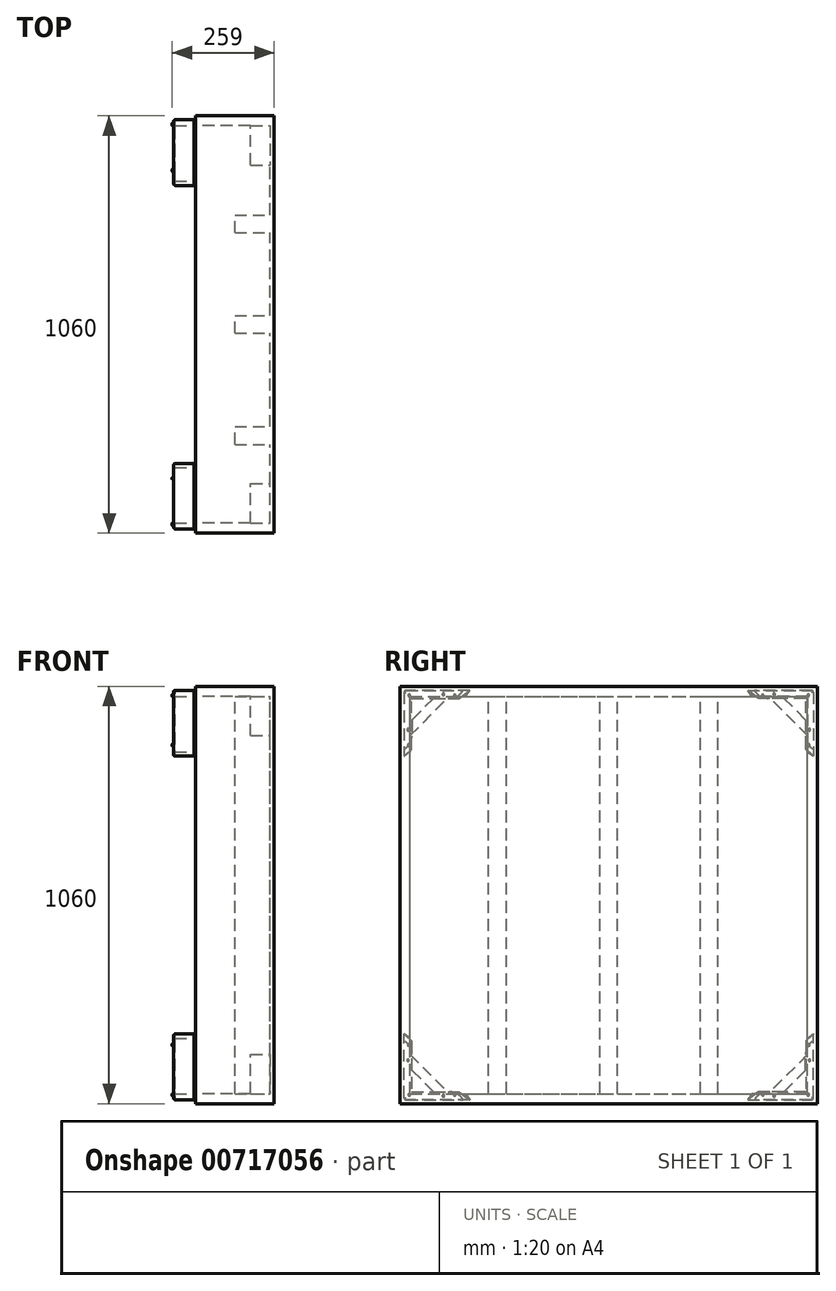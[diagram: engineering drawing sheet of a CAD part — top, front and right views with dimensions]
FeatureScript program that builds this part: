
annotation { "Feature Type Name" : "Feature", "Feature Type Description" : "" }
export const myFeature = defineFeature(function(context is Context, id is Id, definition is map)
    precondition{}
    {
        {
            var Q0;
            Q0=qCreatedBy(makeId("Right.planeOp"),FACE);
            var sketch = newSketch(context, id + "F0", { "sketchPlane" : qUnion([Q0])});
            skLineSegment(sketch, "E0.bottom", {"start": v(530, -530) * mm, "end": v(-530, -530) * mm});
            skLineSegment(sketch, "E0.top", {"start": v(530, 530) * mm, "end": v(-530, 530) * mm});
            skLineSegment(sketch, "E0.left", {"start": v(530, -530) * mm, "end": v(530, 530) * mm});
            skLineSegment(sketch, "E0.right", {"start": v(-530, -530) * mm, "end": v(-530, 530) * mm});
            skPoint(sketch, "E0.middle", {"position": v(0, 0) * mm});
            skSolve(sketch);
        }
        {
            var Q0;
            Q0 = qSketchRegion(id + "F0", true);
            extrude(context, id + "F1", {"entities" : qUnion([Q0]), "depth" : 200 * mm, "offsetDistance" : 25 * mm});
        }
        {
            var Q0;
            Q0=makeQuery(id+"F1.opExtrude","CAP_FACE",FACE,{"disambiguationData":[OSD([sQuery(id+"F0.wireOp",EDGE,"E0.bottom"),sQuery(id+"F0.wireOp",EDGE,"E0.top"),sQuery(id+"F0.wireOp",EDGE,"E0.left"),sQuery(id+"F0.wireOp",EDGE,"E0.right")])],"isStart":true});
            var sketch = newSketch(context, id + "F2", { "sketchPlane" : qUnion([Q0])});
            skLineSegment(sketch, "E1.bottom", {"start": v(505, -505) * mm, "end": v(-505, -505) * mm});
            skLineSegment(sketch, "E1.top", {"start": v(505, 505) * mm, "end": v(-505, 505) * mm});
            skLineSegment(sketch, "E1.left", {"start": v(505, -505) * mm, "end": v(505, 505) * mm});
            skLineSegment(sketch, "E1.right", {"start": v(-505, -505) * mm, "end": v(-505, 505) * mm});
            skPoint(sketch, "E1.middle", {"position": v(0, 0) * mm});
            skSolve(sketch);
        }
        {
            var Q0;
            Q0 = qSketchRegion(id + "F2", true);
            extrude(context, id + "F3", {"entities" : qUnion([Q0]), "operationType" : NewBodyOperationType.REMOVE, "oppositeDirection" : true, "depth" : 190 * mm, "offsetDistance" : 25 * mm});
        }
        {
            var Q0;
            Q0=makeQuery(id+"F3.boolean.opBoolean","COPY",FACE,{"derivedFrom":makeQuery(id+"F3.opExtrude","CAP_FACE",FACE,{"disambiguationData":[OSD([sQuery(id+"F2.wireOp",EDGE,"E1.bottom"),sQuery(id+"F2.wireOp",EDGE,"E1.top"),sQuery(id+"F2.wireOp",EDGE,"E1.left"),sQuery(id+"F2.wireOp",EDGE,"E1.right")])],"isStart":false})});
            var sketch = newSketch(context, id + "F4", { "sketchPlane" : qUnion([Q0])});
            skLineSegment(sketch, "E2", {"start": v(0, 505) * mm, "end": v(0, -505) * mm, "construction": true});
            skLineSegment(sketch, "E3", {"start": v(-505, 0) * mm, "end": v(505, 0) * mm, "construction": true});
            skLineSegment(sketch, "E4", {"start": v(-505, 405) * mm, "end": v(-405, 505) * mm});
            skLineSegment(sketch, "E5", {"start": v(-405, 505) * mm, "end": v(-505, 505) * mm});
            skLineSegment(sketch, "E6", {"start": v(-505, 505) * mm, "end": v(-505, 405) * mm});
            skLineSegment(sketch, "E7.MirrorCS", {"start": v(505, 405) * mm, "end": v(405, 505) * mm});
            skLineSegment(sketch, "E8.MirrorCS", {"start": v(405, 505) * mm, "end": v(505, 505) * mm});
            skLineSegment(sketch, "E9.MirrorCS", {"start": v(505, 505) * mm, "end": v(505, 405) * mm});
            skLineSegment(sketch, "E10.MirrorCS", {"start": v(-505, -405) * mm, "end": v(-405, -505) * mm});
            skLineSegment(sketch, "E11.MirrorCS", {"start": v(-405, -505) * mm, "end": v(-505, -505) * mm});
            skLineSegment(sketch, "E12.MirrorCS", {"start": v(-505, -505) * mm, "end": v(-505, -405) * mm});
            skLineSegment(sketch, "E13.MirrorCS", {"start": v(505, -405) * mm, "end": v(405, -505) * mm});
            skLineSegment(sketch, "E14.MirrorCS", {"start": v(405, -505) * mm, "end": v(505, -505) * mm});
            skLineSegment(sketch, "E15.MirrorCS", {"start": v(505, -505) * mm, "end": v(505, -405) * mm});
            skSolve(sketch);
        }
        {
            var Q0;
            Q0 = qSketchRegion(id + "F4", true);
            extrude(context, id + "F5", {"entities" : qUnion([Q0]), "operationType" : NewBodyOperationType.ADD, "depth" : 50 * mm, "offsetDistance" : 25 * mm});
        }
        {
            var Q0;
            Q0=makeQuery(id+"F5.boolean.opBoolean","MERGE",FACE,{"derivedFrom":[makeQuery(id+"F1.opExtrude","CAP_FACE",FACE,{"disambiguationData":[OSD([sQuery(id+"F0.wireOp",EDGE,"E0.bottom"),sQuery(id+"F0.wireOp",EDGE,"E0.top"),sQuery(id+"F0.wireOp",EDGE,"E0.left"),sQuery(id+"F0.wireOp",EDGE,"E0.right")])],"isStart":true}),makeQuery(id+"F5.opExtrude","CAP_FACE",FACE,{"disambiguationData":[OSD([sQuery(id+"F4.wireOp",EDGE,"E4"),sQuery(id+"F4.wireOp",EDGE,"E5"),sQuery(id+"F4.wireOp",EDGE,"E6")])],"isStart":false}),makeQuery(id+"F5.opExtrude","CAP_FACE",FACE,{"disambiguationData":[OSD([sQuery(id+"F4.wireOp",EDGE,"E7.MirrorCS"),sQuery(id+"F4.wireOp",EDGE,"E8.MirrorCS"),sQuery(id+"F4.wireOp",EDGE,"E9.MirrorCS")])],"isStart":false}),makeQuery(id+"F5.opExtrude","CAP_FACE",FACE,{"disambiguationData":[OSD([sQuery(id+"F4.wireOp",EDGE,"E10.MirrorCS"),sQuery(id+"F4.wireOp",EDGE,"E11.MirrorCS"),sQuery(id+"F4.wireOp",EDGE,"E12.MirrorCS")])],"isStart":false}),makeQuery(id+"F5.opExtrude","CAP_FACE",FACE,{"disambiguationData":[OSD([sQuery(id+"F4.wireOp",EDGE,"E13.MirrorCS"),sQuery(id+"F4.wireOp",EDGE,"E14.MirrorCS"),sQuery(id+"F4.wireOp",EDGE,"E15.MirrorCS")])],"isStart":false})]});
            var sketch = newSketch(context, id + "F6", { "sketchPlane" : qUnion([Q0])});
            skLineSegment(sketch, "E16", {"start": v(-520, 520) * mm, "end": v(-370, 520) * mm});
            skLineSegment(sketch, "E17", {"start": v(-520, 520) * mm, "end": v(-520, 370) * mm});
            skLineSegment(sketch, "E18", {"start": v(-500, 445) * mm, "end": v(-500, 404.8) * mm});
            skLineSegment(sketch, "E19", {"start": v(-520, 370) * mm, "end": v(-517.3, 371.86) * mm});
            skPoint(sketch, "E20.visualSharp", {"position": v(-500, 383.78) * mm});
            skArc(sketch, "E20.filletArc", {"start": v(-517.3, 371.86) * mm, "mid": v(-504.59, 386.2) * mm, "end": v(-500, 404.8) * mm});
            skLineSegment(sketch, "E21", {"start": v(-520, 520) * mm, "end": v(-344.75, 344.75) * mm, "construction": true});
            skLineSegment(sketch, "E22.MirrorCS", {"start": v(-445, 500) * mm, "end": v(-404.8, 500) * mm});
            skArc(sketch, "E23.MirrorCS", {"start": v(-371.86, 517.3) * mm, "mid": v(-386.2, 504.59) * mm, "end": v(-404.8, 500) * mm});
            skLineSegment(sketch, "E24", {"start": v(-371.86, 517.3) * mm, "end": v(-370, 520) * mm});
            skLineSegment(sketch, "E25", {"start": v(-445, 500) * mm, "end": v(-500, 445) * mm});
            skLineSegment(sketch, "E26", {"start": v(0, 530) * mm, "end": v(0, -530) * mm, "construction": true});
            skLineSegment(sketch, "E27", {"start": v(530, 0) * mm, "end": v(-530, 0) * mm, "construction": true});
            skSolve(sketch);
        }
        {
            var Q0;
            Q0 = qSketchRegion(id + "F6", true);
            extrude(context, id + "F7", {"entities" : qUnion([Q0]), "operationType" : NewBodyOperationType.ADD, "depth" : 3 * mm, "offsetDistance" : 25 * mm});
        }
        {
            var Q0;
            Q0=makeQuery(id+"F7.opExtrude","CAP_FACE",FACE,{"disambiguationData":[OSD([sQuery(id+"F6.wireOp",EDGE,"E16"),sQuery(id+"F6.wireOp",EDGE,"E17"),sQuery(id+"F6.wireOp",EDGE,"E18"),sQuery(id+"F6.wireOp",EDGE,"E19"),sQuery(id+"F6.wireOp",EDGE,"E20.filletArc"),sQuery(id+"F6.wireOp",EDGE,"E22.MirrorCS"),sQuery(id+"F6.wireOp",EDGE,"E23.MirrorCS"),sQuery(id+"F6.wireOp",EDGE,"E24"),sQuery(id+"F6.wireOp",EDGE,"E25")])],"isStart":false});
            var sketch = newSketch(context, id + "F8", { "sketchPlane" : qUnion([Q0])});
            skCircle(sketch, "E28", {"center": v(-510, 420) * mm, "radius": 2.75 * mm});
            skCircle(sketch, "E29", {"center": v(-420, 510) * mm, "radius": 3.18 * mm});
            skCircle(sketch, "E30.MirrorC", {"center": v(510, 420) * mm, "radius": 2.75 * mm});
            skCircle(sketch, "E31.MirrorC", {"center": v(420, 510) * mm, "radius": 3.18 * mm});
            skSolve(sketch);
        }
        {
            var Q0;
            Q0=makeQuery(id+"F8.imprint","IMPRINT",FACE,{"disambiguationData":[TD([[makeQuery(id+"F8.imprint","IMPRINT",EDGE,{"derivedFrom":sQuery(id+"F8.wireOp",EDGE,"E28")}),1.0]])]});
            var Q1;
            Q1=makeQuery(id+"F8.imprint","IMPRINT",FACE,{"disambiguationData":[TD([[makeQuery(id+"F8.imprint","IMPRINT",EDGE,{"derivedFrom":sQuery(id+"F8.wireOp",EDGE,"E29")}),1.0]])]});
            extrude(context, id + "F9", {"entities" : qUnion([Q0, Q1]), "operationType" : NewBodyOperationType.REMOVE, "oppositeDirection" : true, "depth" : 25 * mm, "offsetDistance" : 25 * mm});
        }
        {
            var Q0;
            Q0=makeQuery(id+"F7.opExtrude","CAP_FACE",FACE,{"disambiguationData":[OSD([sQuery(id+"F6.wireOp",EDGE,"E16"),sQuery(id+"F6.wireOp",EDGE,"E17"),sQuery(id+"F6.wireOp",EDGE,"E18"),sQuery(id+"F6.wireOp",EDGE,"E19"),sQuery(id+"F6.wireOp",EDGE,"E20.filletArc"),sQuery(id+"F6.wireOp",EDGE,"E22.MirrorCS"),sQuery(id+"F6.wireOp",EDGE,"E23.MirrorCS"),sQuery(id+"F6.wireOp",EDGE,"E24"),sQuery(id+"F6.wireOp",EDGE,"E25")])],"isStart":false});
            var sketch = newSketch(context, id + "F10", { "sketchPlane" : qUnion([Q0])});
            skLineSegment(sketch, "E32", {"start": v(0, 0) * mm, "end": v(0, 553) * mm});
            skLineSegment(sketch, "E33", {"start": v(0, 553) * mm, "end": v(0, -610.23) * mm, "construction": true});
            skLineSegment(sketch, "E34", {"start": v(0, 0) * mm, "end": v(-602.07, 0) * mm});
            skLineSegment(sketch, "E35", {"start": v(-602.07, 0) * mm, "end": v(591.35, 0) * mm, "construction": true});
            skSolve(sketch);
        }
        {
            var Q0;
            Q0=makeQuery(id+"F10.imprint","IMPRINT",FACE,{"disambiguationData":[TD([[makeQuery(id+"F10.imprint","IMPRINT",EDGE,{"derivedFrom":makeQuery(id+"F7.opExtrude","CAP_EDGE",EDGE,{"disambiguationData":[OSD([sQuery(id+"F6.wireOp",EDGE,"E16")])],"isStart":false})}),-1.0]])]});
            var sketch = newSketch(context, id + "F11", { "sketchPlane" : qUnion([Q0])});
            skLineSegment(sketch, "E36", {"start": v(-504.96, 505.02) * mm, "end": v(-363.52, 505.02) * mm});
            skLineSegment(sketch, "E37", {"start": v(-363.52, 505.02) * mm, "end": v(-353.08, 520.03) * mm});
            skLineSegment(sketch, "E38", {"start": v(-353.08, 520.03) * mm, "end": v(-519.88, 520.11) * mm});
            skLineSegment(sketch, "E39", {"start": v(-519.88, 520.11) * mm, "end": v(-519.97, 352.84) * mm});
            skLineSegment(sketch, "E40", {"start": v(-504.96, 505.02) * mm, "end": v(-505.04, 363.57) * mm});
            skLineSegment(sketch, "E41", {"start": v(-505.04, 363.57) * mm, "end": v(-519.97, 352.84) * mm});
            skSolve(sketch);
        }
        {
            var Q0;
            Q0 = qSketchRegion(id + "F11", true);
            extrude(context, id + "F12", {"entities" : qUnion([Q0]), "operationType" : NewBodyOperationType.ADD, "depth" : 50 * mm, "offsetDistance" : 25 * mm});
        }
        {
            var Q0;
            Q0=makeQuery(id+"F12.opExtrude","CAP_FACE",FACE,{"disambiguationData":[OSD([sQuery(id+"F11.wireOp",EDGE,"E36"),sQuery(id+"F11.wireOp",EDGE,"E37"),sQuery(id+"F11.wireOp",EDGE,"E38"),sQuery(id+"F11.wireOp",EDGE,"E39"),sQuery(id+"F11.wireOp",EDGE,"E40"),sQuery(id+"F11.wireOp",EDGE,"E41")])],"isStart":false});
            var sketch = newSketch(context, id + "F13", { "sketchPlane" : qUnion([Q0])});
            skLineSegment(sketch, "E42", {"start": v(-519.97, 352.84) * mm, "end": v(-500.96, 370.22) * mm});
            skLineSegment(sketch, "E43", {"start": v(-500.96, 370.22) * mm, "end": v(-500.96, 500.08) * mm});
            skLineSegment(sketch, "E44", {"start": v(-500.96, 500.08) * mm, "end": v(-380.13, 500.08) * mm});
            skLineSegment(sketch, "E45", {"start": v(-380.13, 500.08) * mm, "end": v(-353.08, 520.03) * mm});
            skLineSegment(sketch, "E46", {"start": v(-353.08, 520.03) * mm, "end": v(-519.88, 520.11) * mm});
            skLineSegment(sketch, "E47", {"start": v(-519.88, 520.11) * mm, "end": v(-519.97, 352.84) * mm});
            skSolve(sketch);
        }
        {
            var Q0;
            Q0 = qSketchRegion(id + "F13", true);
            extrude(context, id + "F14", {"entities" : qUnion([Q0]), "operationType" : NewBodyOperationType.ADD, "depth" : 3 * mm, "offsetDistance" : 25 * mm});
        }
        {
            var Q0;
            Q0=makeQuery(id+"F14.opExtrude","CAP_EDGE",EDGE,{"disambiguationData":[OSD([sQuery(id+"F13.wireOp",EDGE,"E46")])],"isStart":false});
            var Q1;
            Q1=makeQuery(id+"F14.opExtrude","CAP_EDGE",EDGE,{"disambiguationData":[OSD([sQuery(id+"F13.wireOp",EDGE,"E47")])],"isStart":false});
            var Q2;
            Q2=makeQuery(id+"F14.boolean.opBoolean","MERGE",EDGE,{"derivedFrom":[makeQuery(id+"F12.opExtrude","SWEPT_EDGE",EDGE,{"disambiguationData":[OSD([sQuery(id+"F11.wireOp",EDGE,"E38"),sQuery(id+"F11.wireOp",EDGE,"E39")])]}),makeQuery(id+"F14.opExtrude","SWEPT_EDGE",EDGE,{"disambiguationData":[OSD([sQuery(id+"F13.wireOp",EDGE,"E46"),sQuery(id+"F13.wireOp",EDGE,"E47")])]})]});
            fillet(context, id + "F15", {"entities" : qUnion([Q0, Q1, Q2]), "radius" : 5 * mm, "tangentPropagation" : true, "allowEdgeOverflow" : false});
        }
        {
            var Q0;
            Q0=makeQuery(id+"F10.imprint","IMPRINT",FACE,{"disambiguationData":[TD([[makeQuery(id+"F10.imprint","IMPRINT",EDGE,{"derivedFrom":makeQuery(id+"F7.opExtrude","CAP_EDGE",EDGE,{"disambiguationData":[OSD([sQuery(id+"F6.wireOp",EDGE,"E16")])],"isStart":false})}),-1.0]])]});
            var sketch = newSketch(context, id + "F16", { "sketchPlane" : qUnion([Q0])});
            skCircle(sketch, "E48", {"center": v(-468.4, 468.74) * mm, "radius": 2.77 * mm});
            skSolve(sketch);
        }
        {
            var Q0;
            Q0 = qSketchRegion(id + "F16", true);
            extrude(context, id + "F17", {"entities" : qUnion([Q0]), "operationType" : NewBodyOperationType.REMOVE, "oppositeDirection" : true, "depth" : 25 * mm, "offsetDistance" : 25 * mm});
        }
        {
            var Q0;
            Q0=makeQuery(id+"F1.opExtrude","SWEPT_BODY",BODY,{"disambiguationData":[OSD([sQuery(id+"F0.wireOp",EDGE,"E0.bottom"),sQuery(id+"F0.wireOp",EDGE,"E0.top"),sQuery(id+"F0.wireOp",EDGE,"E0.left"),sQuery(id+"F0.wireOp",EDGE,"E0.right")])]});
            var Q1;
            Q1=qCreatedBy(makeId("Front.planeOp"),FACE);
            mirror(context, id + "F18", {"operationType" : NewBodyOperationType.ADD, "entities" : qUnion([Q0]), "mirrorPlane" : qUnion([Q1])});
        }
        {
            var Q0;
            Q0=makeQuery(id+"F1.opExtrude","SWEPT_BODY",BODY,{"disambiguationData":[OSD([sQuery(id+"F0.wireOp",EDGE,"E0.bottom"),sQuery(id+"F0.wireOp",EDGE,"E0.top"),sQuery(id+"F0.wireOp",EDGE,"E0.left"),sQuery(id+"F0.wireOp",EDGE,"E0.right")])]});
            var Q1;
            Q1=qCreatedBy(makeId("Top.planeOp"),FACE);
            mirror(context, id + "F19", {"operationType" : NewBodyOperationType.ADD, "entities" : qUnion([Q0]), "mirrorPlane" : qUnion([Q1])});
        }
        {
            var Q0;
            Q0=makeQuery(id+"F3.boolean.opBoolean","COPY",FACE,{"derivedFrom":makeQuery(id+"F3.opExtrude","CAP_FACE",FACE,{"disambiguationData":[OSD([sQuery(id+"F2.wireOp",EDGE,"E1.bottom"),sQuery(id+"F2.wireOp",EDGE,"E1.top"),sQuery(id+"F2.wireOp",EDGE,"E1.left"),sQuery(id+"F2.wireOp",EDGE,"E1.right")])],"isStart":false})});
            var sketch = newSketch(context, id + "F20", { "sketchPlane" : qUnion([Q0])});
            skLineSegment(sketch, "E49.bottom", {"start": v(22.5, -505) * mm, "end": v(-22.5, -505) * mm});
            skLineSegment(sketch, "E49.top", {"start": v(22.5, 505) * mm, "end": v(-22.5, 505) * mm});
            skLineSegment(sketch, "E49.left", {"start": v(22.5, -505) * mm, "end": v(22.5, 505) * mm});
            skLineSegment(sketch, "E49.right", {"start": v(-22.5, -505) * mm, "end": v(-22.5, 505) * mm});
            skPoint(sketch, "E49.middle", {"position": v(0, 0) * mm});
            skLineSegment(sketch, "E50.bottom", {"start": v(305, -505) * mm, "end": v(260, -505) * mm});
            skLineSegment(sketch, "E50.top", {"start": v(305, 505) * mm, "end": v(260, 505) * mm});
            skLineSegment(sketch, "E50.left", {"start": v(305, -505) * mm, "end": v(305, 505) * mm});
            skLineSegment(sketch, "E50.right", {"start": v(260, -505) * mm, "end": v(260, 505) * mm});
            skPoint(sketch, "E50.middle", {"position": v(282.5, 0) * mm});
            skLineSegment(sketch, "E51.bottom", {"start": v(-232.5, -505) * mm, "end": v(-277.5, -505) * mm});
            skLineSegment(sketch, "E51.top", {"start": v(-232.5, 505) * mm, "end": v(-277.5, 505) * mm});
            skLineSegment(sketch, "E51.left", {"start": v(-232.5, -505) * mm, "end": v(-232.5, 505) * mm});
            skLineSegment(sketch, "E51.right", {"start": v(-277.5, -505) * mm, "end": v(-277.5, 505) * mm});
            skPoint(sketch, "E51.middle", {"position": v(-255, 0) * mm});
            skSolve(sketch);
        }
        {
            var Q0;
            Q0 = qSketchRegion(id + "F20", true);
            extrude(context, id + "F21", {"entities" : qUnion([Q0]), "operationType" : NewBodyOperationType.ADD, "depth" : 90 * mm, "offsetDistance" : 25 * mm});
        }
        {
            var Q0;
            Q0=makeQuery(id+"F18.opPattern","COPY",FACE,{"derivedFrom":makeQuery(id+"F14.opExtrude","CAP_FACE",FACE,{"disambiguationData":[OSD([sQuery(id+"F13.wireOp",EDGE,"E42"),sQuery(id+"F13.wireOp",EDGE,"E43"),sQuery(id+"F13.wireOp",EDGE,"E44"),sQuery(id+"F13.wireOp",EDGE,"E45"),sQuery(id+"F13.wireOp",EDGE,"E46"),sQuery(id+"F13.wireOp",EDGE,"E47")])],"isStart":false}),"instanceName":"1"});
            var sketch = newSketch(context, id + "F22", { "sketchPlane" : qUnion([Q0])});
            skCircle(sketch, "E52", {"center": v(391.23, 507.06) * mm, "radius": 3 * mm});
            skCircle(sketch, "E53", {"center": v(506.83, 507.3) * mm, "radius": 3 * mm});
            skCircle(sketch, "E54", {"center": v(508.54, 380.79) * mm, "radius": 3 * mm});
            skCircle(sketch, "E55.MirrorC", {"center": v(-391.23, 507.06) * mm, "radius": 3 * mm});
            skCircle(sketch, "E56.MirrorC", {"center": v(-506.83, 507.3) * mm, "radius": 3 * mm});
            skCircle(sketch, "E57.MirrorC", {"center": v(-508.54, 380.79) * mm, "radius": 3 * mm});
            skCircle(sketch, "E58.MirrorC", {"center": v(-508.54, -380.79) * mm, "radius": 3 * mm});
            skCircle(sketch, "E59.MirrorC", {"center": v(-506.83, -507.3) * mm, "radius": 3 * mm});
            skCircle(sketch, "E60.MirrorC", {"center": v(-391.23, -507.06) * mm, "radius": 3 * mm});
            skCircle(sketch, "E61.MirrorC", {"center": v(508.54, -380.79) * mm, "radius": 3 * mm});
            skCircle(sketch, "E62.MirrorC", {"center": v(506.83, -507.3) * mm, "radius": 3 * mm});
            skCircle(sketch, "E63.MirrorC", {"center": v(391.23, -507.06) * mm, "radius": 3 * mm});
            skSolve(sketch);
        }
        {
            var Q0;
            Q0 = qSketchRegion(id + "F22", true);
            extrude(context, id + "F23", {"entities" : qUnion([Q0]), "operationType" : NewBodyOperationType.ADD, "depth" : 3 * mm, "offsetDistance" : 25 * mm, "hasDraft" : true, "draftAngle" : 3 * degree, "draftPullDirection" : true});
        }
        {
            var Q0;
            Q0=makeQuery(id+"F23.opExtrude","CAP_EDGE",EDGE,{"disambiguationData":[OSD([sQuery(id+"F22.wireOp",EDGE,"E63.MirrorC")])],"isStart":false});
            var Q1;
            Q1=makeQuery(id+"F23.opExtrude","CAP_EDGE",EDGE,{"disambiguationData":[OSD([sQuery(id+"F22.wireOp",EDGE,"E62.MirrorC")])],"isStart":false});
            var Q2;
            Q2=makeQuery(id+"F23.opExtrude","CAP_EDGE",EDGE,{"disambiguationData":[OSD([sQuery(id+"F22.wireOp",EDGE,"E61.MirrorC")])],"isStart":false});
            var Q3;
            Q3=makeQuery(id+"F23.opExtrude","CAP_EDGE",EDGE,{"disambiguationData":[OSD([sQuery(id+"F22.wireOp",EDGE,"E54")])],"isStart":false});
            var Q4;
            Q4=makeQuery(id+"F23.opExtrude","CAP_EDGE",EDGE,{"disambiguationData":[OSD([sQuery(id+"F22.wireOp",EDGE,"E53")])],"isStart":false});
            var Q5;
            Q5=makeQuery(id+"F23.opExtrude","CAP_EDGE",EDGE,{"disambiguationData":[OSD([sQuery(id+"F22.wireOp",EDGE,"E52")])],"isStart":false});
            var Q6;
            Q6=makeQuery(id+"F23.opExtrude","CAP_EDGE",EDGE,{"disambiguationData":[OSD([sQuery(id+"F22.wireOp",EDGE,"E55.MirrorC")])],"isStart":false});
            var Q7;
            Q7=makeQuery(id+"F23.opExtrude","CAP_EDGE",EDGE,{"disambiguationData":[OSD([sQuery(id+"F22.wireOp",EDGE,"E56.MirrorC")])],"isStart":false});
            var Q8;
            Q8=makeQuery(id+"F23.opExtrude","CAP_EDGE",EDGE,{"disambiguationData":[OSD([sQuery(id+"F22.wireOp",EDGE,"E57.MirrorC")])],"isStart":false});
            var Q9;
            Q9=makeQuery(id+"F23.opExtrude","CAP_EDGE",EDGE,{"disambiguationData":[OSD([sQuery(id+"F22.wireOp",EDGE,"E60.MirrorC")])],"isStart":false});
            var Q10;
            Q10=makeQuery(id+"F23.opExtrude","CAP_EDGE",EDGE,{"disambiguationData":[OSD([sQuery(id+"F22.wireOp",EDGE,"E59.MirrorC")])],"isStart":false});
            var Q11;
            Q11=makeQuery(id+"F23.opExtrude","CAP_EDGE",EDGE,{"disambiguationData":[OSD([sQuery(id+"F22.wireOp",EDGE,"E58.MirrorC")])],"isStart":false});
            fillet(context, id + "F24", {"entities" : qUnion([Q0, Q1, Q2, Q3, Q4, Q5, Q6, Q7, Q8, Q9, Q10, Q11]), "radius" : 1 * mm, "tangentPropagation" : true, "allowEdgeOverflow" : false});
        }
        {
            var Q0;
            Q0=makeQuery(id+"F7.opExtrude","SWEPT_EDGE",EDGE,{"disambiguationData":[OSD([sQuery(id+"F6.wireOp",EDGE,"E16"),sQuery(id+"F6.wireOp",EDGE,"E17")])]});
            var Q1;
            Q1=makeQuery(id+"F18.opPattern","COPY",EDGE,{"derivedFrom":makeQuery(id+"F7.opExtrude","SWEPT_EDGE",EDGE,{"disambiguationData":[OSD([sQuery(id+"F6.wireOp",EDGE,"E16"),sQuery(id+"F6.wireOp",EDGE,"E17")])]}),"instanceName":"1"});
            var Q2;
            {var subQ0=sQuery(id+"F13.wireOp",EDGE,"E47");Q2=makeQuery(id+"F18.opPattern","COPY",EDGE,{"derivedFrom":makeQuery(id+"F15.opFillet","BLEND_EDGE",EDGE,{"blendedFrom":[makeQuery(id+"F14.opExtrude","CAP_EDGE",EDGE,{"disambiguationData":[OSD([subQ0])],"isStart":false}),makeQuery(id+"F14.opExtrude","CAP_FACE",FACE,{"disambiguationData":[OSD([sQuery(id+"F13.wireOp",EDGE,"E42"),sQuery(id+"F13.wireOp",EDGE,"E43"),sQuery(id+"F13.wireOp",EDGE,"E44"),sQuery(id+"F13.wireOp",EDGE,"E45"),sQuery(id+"F13.wireOp",EDGE,"E46"),subQ0])],"isStart":false})],"blendedInto":[makeQuery(id+"F14.opExtrude","CAP_FACE",FACE,{"disambiguationData":[OSD([sQuery(id+"F13.wireOp",EDGE,"E42"),sQuery(id+"F13.wireOp",EDGE,"E43"),sQuery(id+"F13.wireOp",EDGE,"E44"),sQuery(id+"F13.wireOp",EDGE,"E45"),sQuery(id+"F13.wireOp",EDGE,"E46"),subQ0])],"isStart":false})]}),"instanceName":"1"});}
            var Q3;
            Q3=makeQuery(id+"F23.opExtrude","CAP_EDGE",EDGE,{"disambiguationData":[OSD([sQuery(id+"F22.wireOp",EDGE,"E54")])],"isStart":true});
            var Q4;
            {var subQ0=sQuery(id+"F22.wireOp",EDGE,"E54");Q4=makeQuery(id+"F24.opFillet","BLEND_EDGE",EDGE,{"blendedFrom":[makeQuery(id+"F23.opExtrude","CAP_EDGE",EDGE,{"disambiguationData":[OSD([subQ0])],"isStart":false}),makeQuery(id+"F23.opExtrude","SWEPT_FACE",FACE,{"disambiguationData":[OSD([subQ0])]})],"blendedInto":[makeQuery(id+"F23.opExtrude","SWEPT_FACE",FACE,{"disambiguationData":[OSD([subQ0])]})]});}
            var Q5;
            Q5=makeQuery(id+"F19.opPattern","COPY",EDGE,{"derivedFrom":makeQuery(id+"F18.opPattern","COPY",EDGE,{"derivedFrom":makeQuery(id+"F7.opExtrude","SWEPT_EDGE",EDGE,{"disambiguationData":[OSD([sQuery(id+"F6.wireOp",EDGE,"E16"),sQuery(id+"F6.wireOp",EDGE,"E17")])]}),"instanceName":"1"}),"instanceName":"1"});
            var Q6;
            Q6=makeQuery(id+"F19.opPattern","COPY",EDGE,{"derivedFrom":makeQuery(id+"F7.opExtrude","SWEPT_EDGE",EDGE,{"disambiguationData":[OSD([sQuery(id+"F6.wireOp",EDGE,"E16"),sQuery(id+"F6.wireOp",EDGE,"E17")])]}),"instanceName":"1"});
            fillet(context, id + "F25", {"entities" : qUnion([Q0, Q1, Q2, Q3, Q4, Q5, Q6]), "radius" : 5 * mm, "tangentPropagation" : true, "allowEdgeOverflow" : false});
        }
    });
